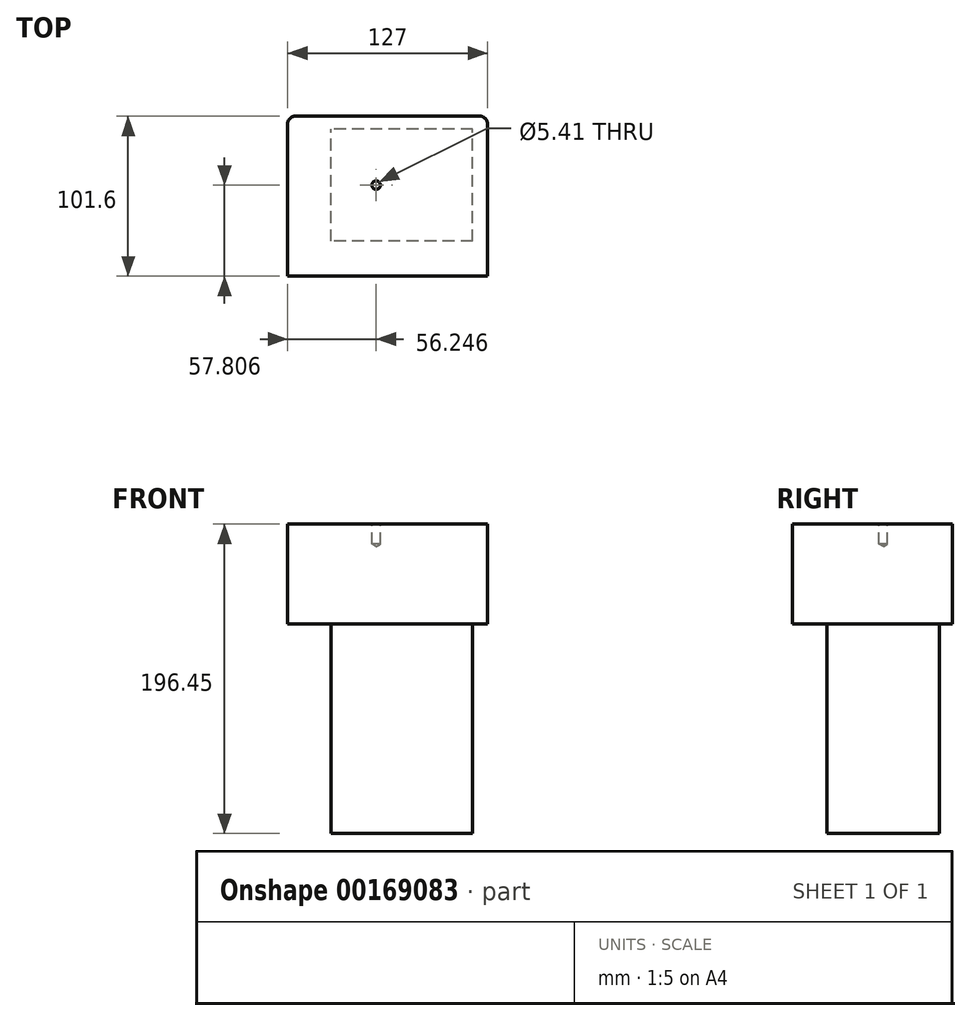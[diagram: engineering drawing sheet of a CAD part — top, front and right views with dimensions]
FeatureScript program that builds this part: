
annotation { "Feature Type Name" : "Feature", "Feature Type Description" : "" }
export const myFeature = defineFeature(function(context is Context, id is Id, definition is map)
    precondition{}
    {
        {
            var Q0;
            Q0=qCreatedBy(makeId("Front.planeOp"),FACE);
            var sketch = newSketch(context, id + "F0", { "sketchPlane" : qUnion([Q0])});
            skLineSegment(sketch, "E0.bottom", {"start": v(-52.23, 17.55) * mm, "end": v(74.77, 17.55) * mm});
            skLineSegment(sketch, "E0.top", {"start": v(-52.23, -45.95) * mm, "end": v(74.77, -45.95) * mm});
            skLineSegment(sketch, "E0.left", {"start": v(-52.23, 17.55) * mm, "end": v(-52.23, -45.95) * mm});
            skLineSegment(sketch, "E0.right", {"start": v(74.77, 17.55) * mm, "end": v(74.77, -45.95) * mm});
            skSolve(sketch);
        }
        {
            var Q0;
            Q0=makeQuery(id+"F0.imprint","IMPRINT",FACE,{"disambiguationData":[TD([[makeQuery(id+"F0.imprint","IMPRINT",EDGE,{"derivedFrom":sQuery(id+"F0.wireOp",EDGE,"E0.bottom")}),-1.0]])]});
            extrude(context, id + "F1", {"entities" : qUnion([Q0]), "endBound" : BoundingType.SYMMETRIC, "depth" : 101.6 * mm});
        }
        {
            var Q0;
            Q0=makeQuery(id+"F1.opExtrude","SWEPT_FACE",FACE,{"disambiguationData":[OSD([sQuery(id+"F0.wireOp",EDGE,"E0.bottom")])]});
            var sketch = newSketch(context, id + "F2", { "sketchPlane" : qUnion([Q0])});
            skPoint(sketch, "E1", {"position": v(4.02, 7) * mm});
            skSolve(sketch);
        }
        {
            var Q0;
            Q0=sQuery(id+"F2.wireOp",VERTEX,"E1");
            var Q1;
            Q1=makeQuery(id+"F1.opExtrude","SWEPT_BODY",BODY,{"disambiguationData":[OSD([sQuery(id+"F0.wireOp",EDGE,"E0.bottom"),sQuery(id+"F0.wireOp",EDGE,"E0.top"),sQuery(id+"F0.wireOp",EDGE,"E0.left"),sQuery(id+"F0.wireOp",EDGE,"E0.right")])]});
            hole(context, id + "F3", {"style" : HoleStyle.SIMPLE, "endStyle" : HoleEndStyle.BLIND, "standardTappedOrClearance" : lookupTablePath({ "standard" : "ANSI", "engagement" : "75%", "pitch" : "28 tpi", "size" : "1/4", "type" : "Tapped" }), "standardBlindInLast" : lookupTablePath({ "standard" : "ANSI", "engagement" : "75%", "pitch" : "28 tpi", "size" : "1/4", "type" : "Tapped" }), "holeDiameter" : 5.4 * mm, "holeDepth" : 12.7 * mm, "locations" : qUnion([Q0]), "scope" : qUnion([Q1]), "majorDiameter" : 6.35 * mm});
        }
        {
            var Q0;
            Q0=makeQuery(id+"F1.opExtrude","SWEPT_FACE",FACE,{"disambiguationData":[OSD([sQuery(id+"F0.wireOp",EDGE,"E0.top")])]});
            var sketch = newSketch(context, id + "F4", { "sketchPlane" : qUnion([Q0])});
            skSolve(sketch);
        }
        {
            var Q0;
            {var subQ0=sQuery(id+"F0.wireOp",EDGE,"E0.top");Q0=makeQuery(id+"F4.imprint","IMPRINT",FACE,{"disambiguationData":[TD([[makeQuery(id+"F4.imprint","IMPRINT",EDGE,{"derivedFrom":makeQuery(id+"F1.opExtrude","CAP_EDGE",EDGE,{"disambiguationData":[OSD([subQ0])],"isStart":true})}),1.0]])]});}
            var sketch = newSketch(context, id + "F6", { "sketchPlane" : qUnion([Q0])});
            skLineSegment(sketch, "E2.bottom", {"start": v(65.25, 28.58) * mm, "end": v(-24.67, 28.58) * mm});
            skLineSegment(sketch, "E2.top", {"start": v(65.25, -42.64) * mm, "end": v(-24.67, -42.64) * mm});
            skLineSegment(sketch, "E2.left", {"start": v(65.25, 28.58) * mm, "end": v(65.25, -42.64) * mm});
            skLineSegment(sketch, "E2.right", {"start": v(-24.67, 28.58) * mm, "end": v(-24.67, -42.64) * mm});
            skSolve(sketch);
        }
        {
            var Q0;
            Q0=makeQuery(id+"F6.imprint","IMPRINT",FACE,{"disambiguationData":[TD([[makeQuery(id+"F6.imprint","IMPRINT",EDGE,{"derivedFrom":sQuery(id+"F6.wireOp",EDGE,"E2.bottom")}),1.0]])]});
            extrude(context, id + "F5", {"entities" : qUnion([Q0]), "operationType" : NewBodyOperationType.ADD, "depth" : 132.95 * mm});
        }
        {
            var Q0;
            Q0=makeQuery(id+"F1.opExtrude","CAP_EDGE",EDGE,{"disambiguationData":[OSD([sQuery(id+"F0.wireOp",EDGE,"E0.right")])],"isStart":true});
            var Q1;
            Q1=makeQuery(id+"F1.opExtrude","CAP_EDGE",EDGE,{"disambiguationData":[OSD([sQuery(id+"F0.wireOp",EDGE,"E0.left")])],"isStart":true});
            fillet(context, id + "F7", {"entities" : qUnion([Q0, Q1]), "radius" : 5 * mm, "tangentPropagation" : true, "allowEdgeOverflow" : false});
        }
    });
